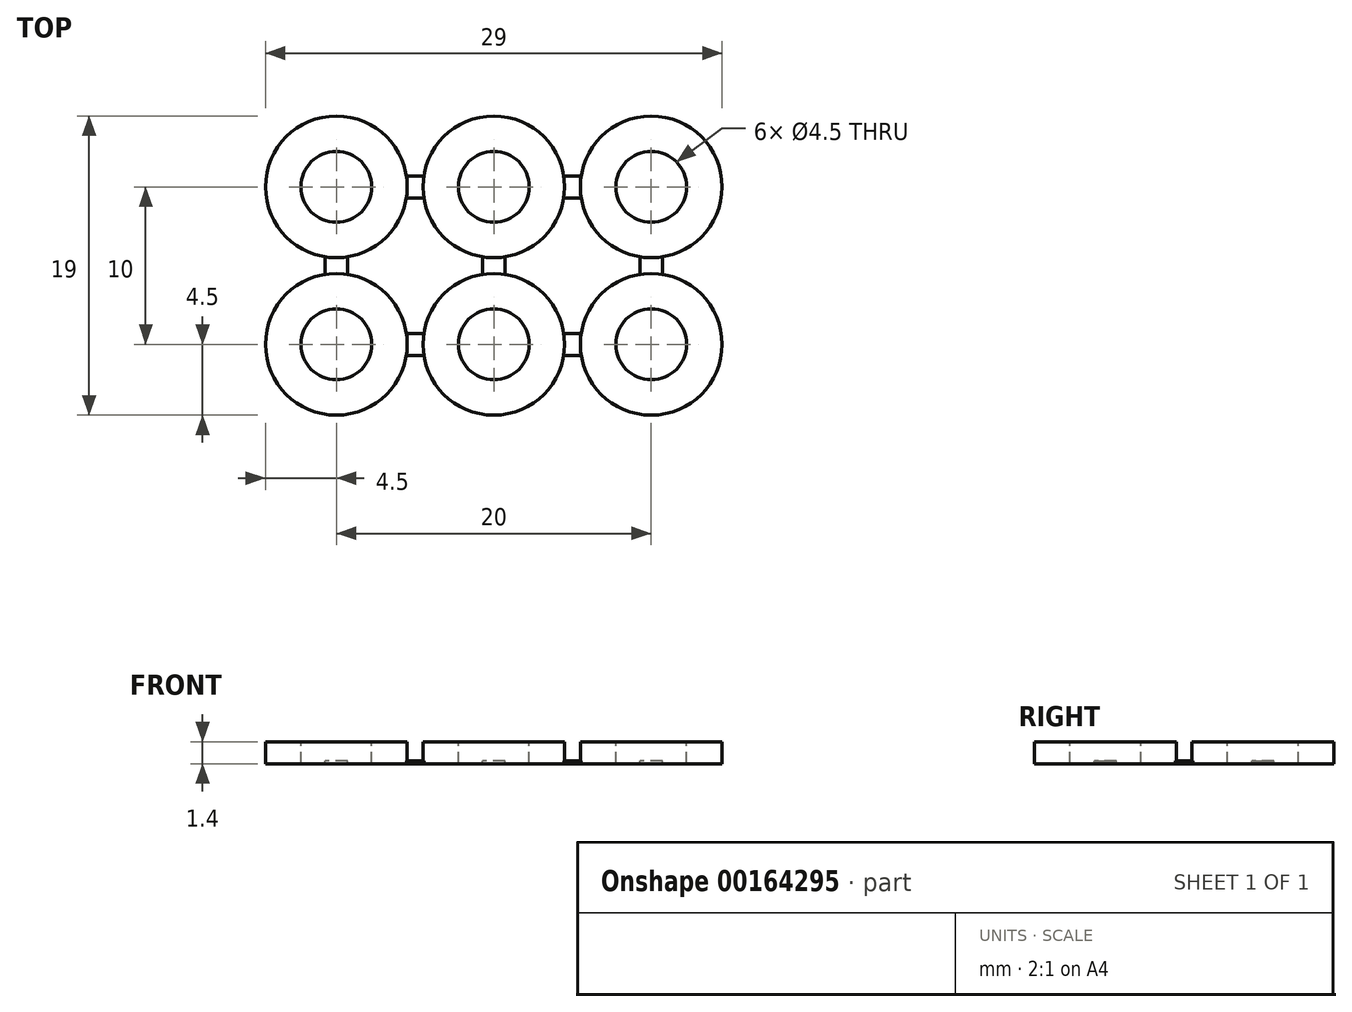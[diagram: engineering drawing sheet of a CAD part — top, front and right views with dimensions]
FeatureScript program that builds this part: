
annotation { "Feature Type Name" : "Feature", "Feature Type Description" : "" }
export const myFeature = defineFeature(function(context is Context, id is Id, definition is map)
    precondition{}
    {
        {
            var Q0;
            Q0=qCreatedBy(makeId("Top.planeOp"),FACE);
            var sketch = newSketch(context, id + "F0", { "sketchPlane" : qUnion([Q0])});
            skCircle(sketch, "E0", {"center": v(0, 0) * mm, "radius": 2.25 * mm});
            skCircle(sketch, "E1", {"center": v(0, 0) * mm, "radius": 4.5 * mm});
            skLineSegment(sketch, "E2", {"start": v(4.5, 0) * mm, "end": v(5.5, 0) * mm, "construction": true});
            skCircle(sketch, "E3", {"center": v(10, 0) * mm, "radius": 4.5 * mm, "construction": true});
            skLineSegment(sketch, "E4", {"start": v(4.45, 0.7) * mm, "end": v(5.55, 0.7) * mm});
            skLineSegment(sketch, "E5.MirrorCS", {"start": v(4.45, -0.7) * mm, "end": v(5.55, -0.7) * mm});
            skLineSegment(sketch, "E6.1.0", {"start": v(0.7, -4.45) * mm, "end": v(0.7, -5.55) * mm});
            skLineSegment(sketch, "E6.1.1", {"start": v(-0.7, -4.45) * mm, "end": v(-0.7, -5.55) * mm});
            skLineSegment(sketch, "E6.2.0", {"start": v(-4.45, -0.7) * mm, "end": v(-5.55, -0.7) * mm});
            skLineSegment(sketch, "E6.2.1", {"start": v(-4.45, 0.7) * mm, "end": v(-5.55, 0.7) * mm});
            skLineSegment(sketch, "E6.anchor1", {"start": v(0, 0) * mm, "end": v(4.45, -0.7) * mm, "construction": true});
            skLineSegment(sketch, "E6.anchor2", {"start": v(0, 0) * mm, "end": v(-4.45, 0.7) * mm, "construction": true});
            skLineSegment(sketch, "E7.0.1.0", {"start": v(4.45, -9.3) * mm, "end": v(5.55, -9.3) * mm});
            skPoint(sketch, "E7.0.1.1", {"position": v(0, -10) * mm});
            skCircle(sketch, "E7.0.1.2", {"center": v(0, -10) * mm, "radius": 4.5 * mm});
            skLineSegment(sketch, "E7.0.1.3", {"start": v(4.5, -10) * mm, "end": v(5.5, -10) * mm, "construction": true});
            skLineSegment(sketch, "E7.0.1.4", {"start": v(4.45, -10.7) * mm, "end": v(5.55, -10.7) * mm});
            skCircle(sketch, "E7.0.1.5", {"center": v(0, -10) * mm, "radius": 2.25 * mm});
            skLineSegment(sketch, "E7.0.1.6", {"start": v(0.7, -14.45) * mm, "end": v(0.7, -15.55) * mm});
            skLineSegment(sketch, "E7.0.1.7", {"start": v(-0.7, -14.45) * mm, "end": v(-0.7, -15.55) * mm});
            skLineSegment(sketch, "E7.0.1.8", {"start": v(0, -10) * mm, "end": v(4.45, -10.7) * mm, "construction": true});
            skLineSegment(sketch, "E7.0.1.9", {"start": v(0, -10) * mm, "end": v(-4.45, -9.3) * mm, "construction": true});
            skLineSegment(sketch, "E7.1.0.0", {"start": v(14.45, 0.7) * mm, "end": v(15.55, 0.7) * mm});
            skCircle(sketch, "E7.1.0.2", {"center": v(10, 0) * mm, "radius": 4.5 * mm});
            skLineSegment(sketch, "E7.1.0.3", {"start": v(14.5, 0) * mm, "end": v(15.5, 0) * mm, "construction": true});
            skLineSegment(sketch, "E7.1.0.4", {"start": v(14.45, -0.7) * mm, "end": v(15.55, -0.7) * mm});
            skCircle(sketch, "E7.1.0.5", {"center": v(10, 0) * mm, "radius": 2.25 * mm});
            skLineSegment(sketch, "E7.1.0.6", {"start": v(10.7, -4.45) * mm, "end": v(10.7, -5.55) * mm});
            skLineSegment(sketch, "E7.1.0.7", {"start": v(9.3, -4.45) * mm, "end": v(9.3, -5.55) * mm});
            skLineSegment(sketch, "E7.1.0.8", {"start": v(10, 0) * mm, "end": v(14.45, -0.7) * mm, "construction": true});
            skLineSegment(sketch, "E7.1.0.9", {"start": v(10, 0) * mm, "end": v(5.55, 0.7) * mm, "construction": true});
            skLineSegment(sketch, "E7.1.1.0", {"start": v(14.45, -9.3) * mm, "end": v(15.55, -9.3) * mm});
            skPoint(sketch, "E7.1.1.1", {"position": v(10, -10) * mm});
            skCircle(sketch, "E7.1.1.2", {"center": v(10, -10) * mm, "radius": 4.5 * mm});
            skLineSegment(sketch, "E7.1.1.3", {"start": v(14.5, -10) * mm, "end": v(15.5, -10) * mm, "construction": true});
            skLineSegment(sketch, "E7.1.1.4", {"start": v(14.45, -10.7) * mm, "end": v(15.55, -10.7) * mm});
            skCircle(sketch, "E7.1.1.5", {"center": v(10, -10) * mm, "radius": 2.25 * mm});
            skLineSegment(sketch, "E7.1.1.6", {"start": v(10.7, -14.45) * mm, "end": v(10.7, -15.55) * mm});
            skLineSegment(sketch, "E7.1.1.7", {"start": v(9.3, -14.45) * mm, "end": v(9.3, -15.55) * mm});
            skLineSegment(sketch, "E7.1.1.8", {"start": v(10, -10) * mm, "end": v(14.45, -10.7) * mm, "construction": true});
            skLineSegment(sketch, "E7.1.1.9", {"start": v(10, -10) * mm, "end": v(5.55, -9.3) * mm, "construction": true});
            skLineSegment(sketch, "E7.2.0.0", {"start": v(24.45, 0.7) * mm, "end": v(25.55, 0.7) * mm});
            skPoint(sketch, "E7.2.0.1", {"position": v(20, 0) * mm});
            skCircle(sketch, "E7.2.0.2", {"center": v(20, 0) * mm, "radius": 4.5 * mm});
            skLineSegment(sketch, "E7.2.0.3", {"start": v(24.5, 0) * mm, "end": v(25.5, 0) * mm, "construction": true});
            skLineSegment(sketch, "E7.2.0.4", {"start": v(24.45, -0.7) * mm, "end": v(25.55, -0.7) * mm});
            skCircle(sketch, "E7.2.0.5", {"center": v(20, 0) * mm, "radius": 2.25 * mm});
            skLineSegment(sketch, "E7.2.0.6", {"start": v(20.7, -4.45) * mm, "end": v(20.7, -5.55) * mm});
            skLineSegment(sketch, "E7.2.0.7", {"start": v(19.3, -4.45) * mm, "end": v(19.3, -5.55) * mm});
            skLineSegment(sketch, "E7.2.0.8", {"start": v(20, 0) * mm, "end": v(24.45, -0.7) * mm, "construction": true});
            skLineSegment(sketch, "E7.2.0.9", {"start": v(20, 0) * mm, "end": v(15.55, 0.7) * mm, "construction": true});
            skLineSegment(sketch, "E7.2.1.0", {"start": v(24.45, -9.3) * mm, "end": v(25.55, -9.3) * mm});
            skPoint(sketch, "E7.2.1.1", {"position": v(20, -10) * mm});
            skCircle(sketch, "E7.2.1.2", {"center": v(20, -10) * mm, "radius": 4.5 * mm});
            skLineSegment(sketch, "E7.2.1.3", {"start": v(24.5, -10) * mm, "end": v(25.5, -10) * mm, "construction": true});
            skLineSegment(sketch, "E7.2.1.4", {"start": v(24.45, -10.7) * mm, "end": v(25.55, -10.7) * mm});
            skCircle(sketch, "E7.2.1.5", {"center": v(20, -10) * mm, "radius": 2.25 * mm});
            skLineSegment(sketch, "E7.2.1.6", {"start": v(20.7, -14.45) * mm, "end": v(20.7, -15.55) * mm});
            skLineSegment(sketch, "E7.2.1.7", {"start": v(19.3, -14.45) * mm, "end": v(19.3, -15.55) * mm});
            skLineSegment(sketch, "E7.2.1.8", {"start": v(20, -10) * mm, "end": v(24.45, -10.7) * mm, "construction": true});
            skLineSegment(sketch, "E7.2.1.9", {"start": v(20, -10) * mm, "end": v(15.55, -9.3) * mm, "construction": true});
            skLineSegment(sketch, "E7.direction1", {"start": v(-0.7, -5.55) * mm, "end": v(9.3, -5.55) * mm, "construction": true});
            skLineSegment(sketch, "E7.direction2", {"start": v(-0.7, -5.55) * mm, "end": v(-0.7, -15.55) * mm, "construction": true});
            skSolve(sketch);
        }
        {
            var Q0;
            {var subQ0=sQuery(id+"F0.wireOp",EDGE,"E6.1.0");Q0=makeQuery(id+"F0.imprint","IMPRINT",FACE,{"disambiguationData":[TD([[makeQuery(id+"F0.imprint","IMPRINT",EDGE,{"derivedFrom":subQ0}),-1.0]])]});}
            var Q1;
            {var subQ0=sQuery(id+"F0.wireOp",EDGE,"E4");Q1=makeQuery(id+"F0.imprint","IMPRINT",FACE,{"disambiguationData":[TD([[makeQuery(id+"F0.imprint","IMPRINT",EDGE,{"derivedFrom":subQ0}),-1.0]])]});}
            var Q2;
            {var subQ0=sQuery(id+"F0.wireOp",EDGE,"E7.0.1.0");Q2=makeQuery(id+"F0.imprint","IMPRINT",FACE,{"disambiguationData":[TD([[makeQuery(id+"F0.imprint","IMPRINT",EDGE,{"derivedFrom":subQ0}),-1.0]])]});}
            var Q3;
            {var subQ0=sQuery(id+"F0.wireOp",EDGE,"E7.1.0.0");Q3=makeQuery(id+"F0.imprint","IMPRINT",FACE,{"disambiguationData":[TD([[makeQuery(id+"F0.imprint","IMPRINT",EDGE,{"derivedFrom":subQ0}),-1.0]])]});}
            var Q4;
            {var subQ0=sQuery(id+"F0.wireOp",EDGE,"E7.1.1.0");Q4=makeQuery(id+"F0.imprint","IMPRINT",FACE,{"disambiguationData":[TD([[makeQuery(id+"F0.imprint","IMPRINT",EDGE,{"derivedFrom":subQ0}),-1.0]])]});}
            var Q5;
            {var subQ0=sQuery(id+"F0.wireOp",EDGE,"E7.2.0.6");Q5=makeQuery(id+"F0.imprint","IMPRINT",FACE,{"disambiguationData":[TD([[makeQuery(id+"F0.imprint","IMPRINT",EDGE,{"derivedFrom":subQ0}),-1.0]])]});}
            var Q6;
            Q6=makeQuery(id+"F0.imprint","IMPRINT",FACE,{"disambiguationData":[TD([[makeQuery(id+"F0.imprint","IMPRINT",EDGE,{"derivedFrom":sQuery(id+"F0.wireOp",EDGE,"E7.0.1.5")}),-1.0]])]});
            var Q7;
            Q7=makeQuery(id+"F0.imprint","IMPRINT",FACE,{"disambiguationData":[TD([[makeQuery(id+"F0.imprint","IMPRINT",EDGE,{"derivedFrom":sQuery(id+"F0.wireOp",EDGE,"E7.2.0.5")}),-1.0]])]});
            var Q8;
            Q8=makeQuery(id+"F0.imprint","IMPRINT",FACE,{"disambiguationData":[TD([[makeQuery(id+"F0.imprint","IMPRINT",EDGE,{"derivedFrom":sQuery(id+"F0.wireOp",EDGE,"E7.2.1.5")}),-1.0]])]});
            var Q9;
            Q9=makeQuery(id+"F0.imprint","IMPRINT",FACE,{"disambiguationData":[TD([[makeQuery(id+"F0.imprint","IMPRINT",EDGE,{"derivedFrom":sQuery(id+"F0.wireOp",EDGE,"E7.1.0.5")}),-1.0]])]});
            var Q10;
            Q10=makeQuery(id+"F0.imprint","IMPRINT",FACE,{"disambiguationData":[TD([[makeQuery(id+"F0.imprint","IMPRINT",EDGE,{"derivedFrom":sQuery(id+"F0.wireOp",EDGE,"E7.1.1.5")}),-1.0]])]});
            var Q11;
            Q11=makeQuery(id+"F0.imprint","IMPRINT",FACE,{"disambiguationData":[TD([[makeQuery(id+"F0.imprint","IMPRINT",EDGE,{"derivedFrom":sQuery(id+"F0.wireOp",EDGE,"E0")}),-1.0]])]});
            var Q12;
            {var subQ0=sQuery(id+"F0.wireOp",EDGE,"E7.1.0.6");Q12=makeQuery(id+"F0.imprint","IMPRINT",FACE,{"disambiguationData":[TD([[makeQuery(id+"F0.imprint","IMPRINT",EDGE,{"derivedFrom":subQ0}),-1.0]])]});}
            extrude(context, id + "F1", {"entities" : qUnion([Q0, Q1, Q2, Q3, Q4, Q5, Q6, Q7, Q8, Q9, Q10, Q11, Q12]), "oppositeDirection" : true, "depth" : .2 * mm});
        }
        {
            var Q0;
            Q0=makeQuery(id+"F0.imprint","IMPRINT",FACE,{"disambiguationData":[TD([[makeQuery(id+"F0.imprint","IMPRINT",EDGE,{"derivedFrom":sQuery(id+"F0.wireOp",EDGE,"E0")}),-1.0]])]});
            var Q1;
            Q1=makeQuery(id+"F0.imprint","IMPRINT",FACE,{"disambiguationData":[TD([[makeQuery(id+"F0.imprint","IMPRINT",EDGE,{"derivedFrom":sQuery(id+"F0.wireOp",EDGE,"E7.1.0.5")}),-1.0]])]});
            var Q2;
            Q2=makeQuery(id+"F0.imprint","IMPRINT",FACE,{"disambiguationData":[TD([[makeQuery(id+"F0.imprint","IMPRINT",EDGE,{"derivedFrom":sQuery(id+"F0.wireOp",EDGE,"E7.2.0.5")}),-1.0]])]});
            var Q3;
            Q3=makeQuery(id+"F0.imprint","IMPRINT",FACE,{"disambiguationData":[TD([[makeQuery(id+"F0.imprint","IMPRINT",EDGE,{"derivedFrom":sQuery(id+"F0.wireOp",EDGE,"E7.2.1.5")}),-1.0]])]});
            var Q4;
            Q4=makeQuery(id+"F0.imprint","IMPRINT",FACE,{"disambiguationData":[TD([[makeQuery(id+"F0.imprint","IMPRINT",EDGE,{"derivedFrom":sQuery(id+"F0.wireOp",EDGE,"E7.1.1.5")}),-1.0]])]});
            var Q5;
            Q5=makeQuery(id+"F0.imprint","IMPRINT",FACE,{"disambiguationData":[TD([[makeQuery(id+"F0.imprint","IMPRINT",EDGE,{"derivedFrom":sQuery(id+"F0.wireOp",EDGE,"E7.0.1.5")}),-1.0]])]});
            extrude(context, id + "F2", {"entities" : qUnion([Q0, Q1, Q2, Q3, Q4, Q5]), "operationType" : NewBodyOperationType.ADD, "depth" : 1.2 * mm});
        }
    });
